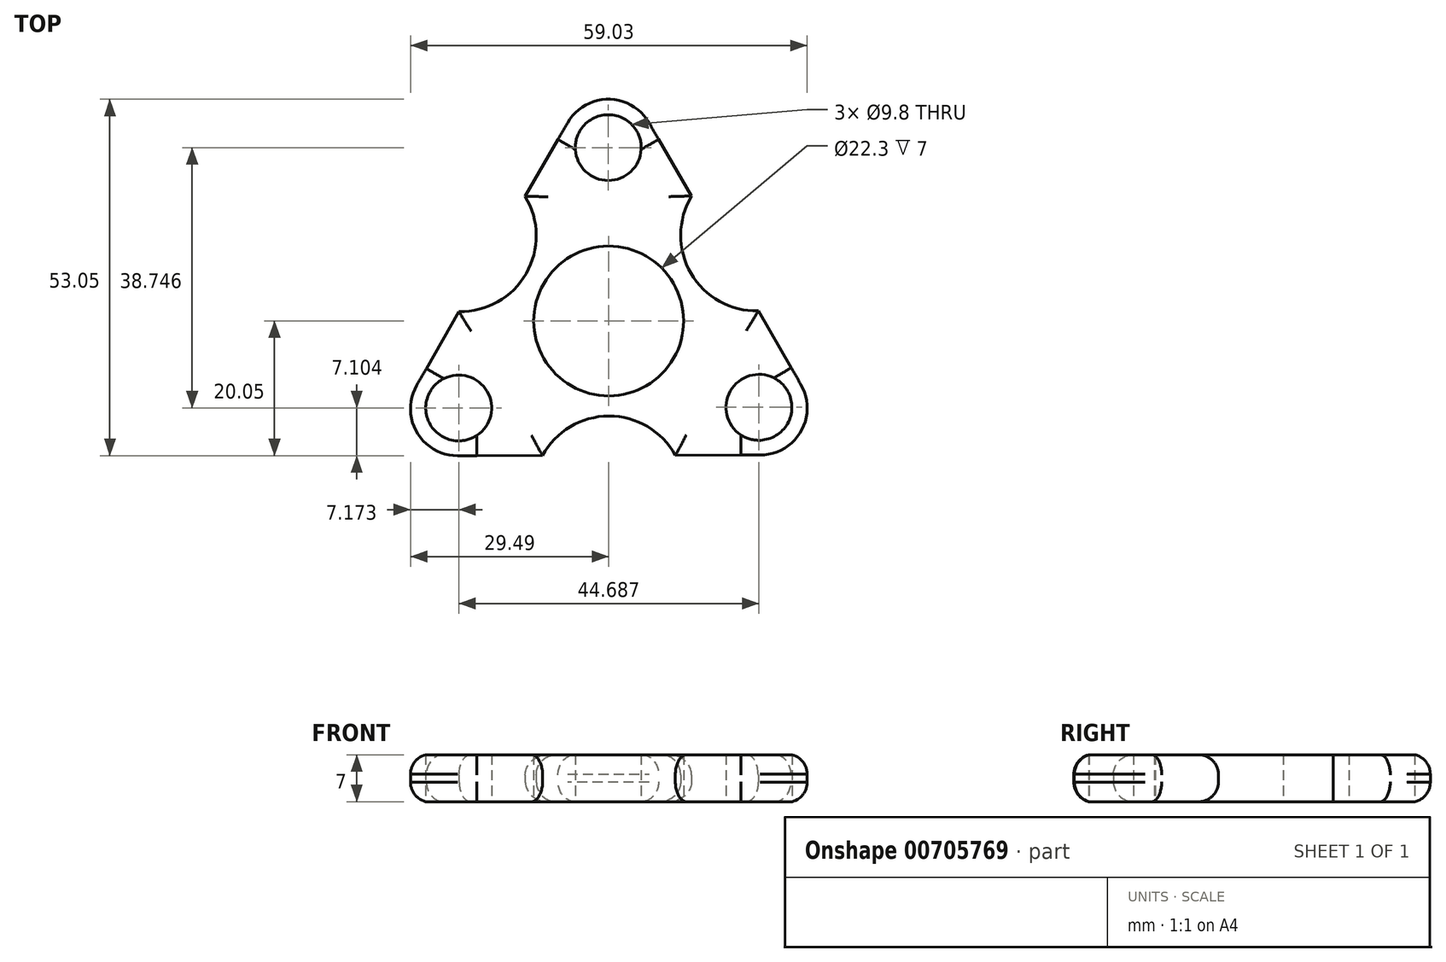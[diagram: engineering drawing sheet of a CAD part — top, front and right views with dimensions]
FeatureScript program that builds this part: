
annotation { "Feature Type Name" : "Feature", "Feature Type Description" : "" }
export const myFeature = defineFeature(function(context is Context, id is Id, definition is map)
    precondition{}
    {
        {
            var Q0;
            Q0=qCreatedBy(makeId("Top.planeOp"),FACE);
            var sketch = newSketch(context, id + "F0", { "sketchPlane" : qUnion([Q0])});
            skCircle(sketch, "E0.cCircle", {"center": v(0, 0) * mm, "radius": 20 * mm, "construction": true});
            skLineSegment(sketch, "E0.0", {"start": v(6, 29.51) * mm, "end": v(28.6, -9.44) * mm});
            skLineSegment(sketch, "E0.1", {"start": v(22.56, -19.95) * mm, "end": v(-22.48, -20.05) * mm});
            skLineSegment(sketch, "E0.2", {"start": v(-28.56, -9.56) * mm, "end": v(-6.12, 29.49) * mm});
            skPoint(sketch, "E0.0.midPoint", {"position": v(17.3, 10.04) * mm});
            skCircle(sketch, "E1", {"center": v(22.37, -12.85) * mm, "radius": 7.1 * mm});
            skCircle(sketch, "E2", {"center": v(22.37, -12.85) * mm, "radius": 4.9 * mm});
            skCircle(sketch, "E3", {"center": v(0, 0) * mm, "radius": 11.15 * mm});
            skArc(sketch, "E4", {"start": v(12.34, 18.58) * mm, "mid": v(12.24, 7.1) * mm, "end": v(22.26, 1.5) * mm});
            skArc(sketch, "E5.1.0", {"start": v(-22.26, 1.4) * mm, "mid": v(-12.27, 7.05) * mm, "end": v(-12.42, 18.53) * mm});
            skPoint(sketch, "E5.1.1", {"position": v(-17.34, 9.96) * mm});
            skCircle(sketch, "E5.1.2", {"center": v(-0.05, 25.8) * mm, "radius": 4.9 * mm});
            skCircle(sketch, "E5.1.3", {"center": v(-0.05, 25.8) * mm, "radius": 7.1 * mm});
            skArc(sketch, "E5.2.0", {"start": v(9.92, -19.98) * mm, "mid": v(0.03, -14.15) * mm, "end": v(-9.83, -20.02) * mm});
            skPoint(sketch, "E5.2.1", {"position": v(0.04, -20) * mm});
            skCircle(sketch, "E5.2.2", {"center": v(-22.32, -12.95) * mm, "radius": 4.9 * mm});
            skCircle(sketch, "E5.2.3", {"center": v(-22.32, -12.95) * mm, "radius": 7.1 * mm});
            skPoint(sketch, "E6.visualSharp", {"position": v(-34.6, -20.07) * mm});
            skArc(sketch, "E6.filletArc", {"start": v(-28.56, -9.56) * mm, "mid": v(-28.54, -16.56) * mm, "end": v(-22.48, -20.05) * mm});
            skPoint(sketch, "E7.visualSharp", {"position": v(-0.08, 40) * mm});
            skArc(sketch, "E7.filletArc", {"start": v(6, 29.51) * mm, "mid": v(-0.07, 33) * mm, "end": v(-6.12, 29.49) * mm});
            skPoint(sketch, "E8.visualSharp", {"position": v(34.68, -19.93) * mm});
            skArc(sketch, "E8.filletArc", {"start": v(22.56, -19.95) * mm, "mid": v(28.61, -16.44) * mm, "end": v(28.6, -9.44) * mm});
            skSolve(sketch);
        }
        {
            var Q0;
            Q0=makeQuery(id+"F0.imprint","IMPRINT",FACE,{"disambiguationData":[TD([[makeQuery(id+"F0.imprint","IMPRINT",EDGE,{"derivedFrom":sQuery(id+"F0.wireOp",EDGE,"E2")}),-1.0]])]});
            var Q1;
            Q1=makeQuery(id+"F0.imprint","IMPRINT",FACE,{"disambiguationData":[TD([[makeQuery(id+"F0.imprint","IMPRINT",EDGE,{"derivedFrom":sQuery(id+"F0.wireOp",EDGE,"E5.1.2")}),-1.0]])]});
            var Q2;
            Q2=makeQuery(id+"F0.imprint","IMPRINT",FACE,{"disambiguationData":[TD([[makeQuery(id+"F0.imprint","IMPRINT",EDGE,{"derivedFrom":sQuery(id+"F0.wireOp",EDGE,"E5.2.2")}),-1.0]])]});
            var Q3;
            {var subQ0=sQuery(id+"F0.wireOp",EDGE,"E8.filletArc");Q3=makeQuery(id+"F0.imprint","IMPRINT",FACE,{"disambiguationData":[TD([[makeQuery(id+"F0.imprint","IMPRINT",EDGE,{"derivedFrom":subQ0}),1.0]])]});}
            var Q4;
            {var subQ0=sQuery(id+"F0.wireOp",EDGE,"E6.filletArc");Q4=makeQuery(id+"F0.imprint","IMPRINT",FACE,{"disambiguationData":[TD([[makeQuery(id+"F0.imprint","IMPRINT",EDGE,{"derivedFrom":subQ0}),1.0]])]});}
            var Q5;
            {var subQ0=sQuery(id+"F0.wireOp",EDGE,"E7.filletArc");Q5=makeQuery(id+"F0.imprint","IMPRINT",FACE,{"disambiguationData":[TD([[makeQuery(id+"F0.imprint","IMPRINT",EDGE,{"derivedFrom":subQ0}),1.0]])]});}
            var Q6;
            Q6=makeQuery(id+"F0.imprint","IMPRINT",FACE,{"disambiguationData":[TD([[makeQuery(id+"F0.imprint","IMPRINT",EDGE,{"derivedFrom":sQuery(id+"F0.wireOp",EDGE,"E3")}),-1.0]])]});
            extrude(context, id + "F1", {"entities" : qUnion([Q0, Q1, Q2, Q3, Q4, Q5, Q6]), "depth" : 7 * mm, "offsetDistance" : 25 * mm});
        }
        {
            var Q0;
            Q0=makeQuery(id+"F1.opExtrude","CAP_EDGE",EDGE,{"disambiguationData":[OSD([sQuery(id+"F0.wireOp",EDGE,"E5.2.0")])],"isStart":false});
            var Q1;
            {var subQ0=sQuery(id+"F0.wireOp",EDGE,"E0.1");Q1=makeQuery(id+"F1.opExtrude","CAP_EDGE",EDGE,{"disambiguationData":[OSD([subQ0]),TDD([makeQuery(id+"F0.imprint","IMPRINT",EDGE,{"disambiguationData":[TD([[makeQuery(id+"F0.imprint","INTERSECT",VERTEX,{"disambiguationData":[OD(1.0)],"derivedFrom":[subQ0,sQuery(id+"F0.wireOp",EDGE,"E5.2.0")]}),-1.0]])],"derivedFrom":subQ0}),makeQuery(id+"F0.imprint","IMPRINT",EDGE,{"disambiguationData":[TD([[makeQuery(id+"F0.imprint","INTERSECT",VERTEX,{"derivedFrom":[subQ0,sQuery(id+"F0.wireOp",EDGE,"E6.filletArc")]}),1.0]])],"derivedFrom":subQ0})])],"isStart":false});}
            var Q2;
            Q2=makeQuery(id+"F1.opExtrude","CAP_EDGE",EDGE,{"disambiguationData":[OSD([sQuery(id+"F0.wireOp",EDGE,"E5.1.0")])],"isStart":false});
            var Q3;
            {var subQ0=sQuery(id+"F0.wireOp",EDGE,"E0.2");Q3=makeQuery(id+"F1.opExtrude","CAP_EDGE",EDGE,{"disambiguationData":[OSD([subQ0]),TDD([makeQuery(id+"F0.imprint","IMPRINT",EDGE,{"disambiguationData":[TD([[makeQuery(id+"F0.imprint","INTERSECT",VERTEX,{"disambiguationData":[OD(1.0)],"derivedFrom":[subQ0,sQuery(id+"F0.wireOp",EDGE,"E5.1.0")]}),-1.0]])],"derivedFrom":subQ0}),makeQuery(id+"F0.imprint","IMPRINT",EDGE,{"disambiguationData":[TD([[makeQuery(id+"F0.imprint","INTERSECT",VERTEX,{"derivedFrom":[subQ0,sQuery(id+"F0.wireOp",EDGE,"E7.filletArc")]}),1.0]])],"derivedFrom":subQ0})])],"isStart":false});}
            var Q4;
            {var subQ0=sQuery(id+"F0.wireOp",EDGE,"E0.0");Q4=makeQuery(id+"F1.opExtrude","CAP_EDGE",EDGE,{"disambiguationData":[OSD([subQ0]),TDD([makeQuery(id+"F0.imprint","IMPRINT",EDGE,{"disambiguationData":[TD([[makeQuery(id+"F0.imprint","INTERSECT",VERTEX,{"disambiguationData":[OD(1.0)],"derivedFrom":[subQ0,sQuery(id+"F0.wireOp",EDGE,"E4")]}),-1.0]])],"derivedFrom":subQ0}),makeQuery(id+"F0.imprint","IMPRINT",EDGE,{"disambiguationData":[TD([[makeQuery(id+"F0.imprint","INTERSECT",VERTEX,{"derivedFrom":[subQ0,sQuery(id+"F0.wireOp",EDGE,"E8.filletArc")]}),1.0]])],"derivedFrom":subQ0})])],"isStart":false});}
            var Q5;
            Q5=makeQuery(id+"F1.opExtrude","CAP_EDGE",EDGE,{"disambiguationData":[OSD([sQuery(id+"F0.wireOp",EDGE,"E4")])],"isStart":false});
            var Q6;
            {var subQ0=sQuery(id+"F0.wireOp",EDGE,"E0.1");Q6=makeQuery(id+"F1.opExtrude","CAP_EDGE",EDGE,{"disambiguationData":[OSD([subQ0]),TDD([makeQuery(id+"F0.imprint","IMPRINT",EDGE,{"disambiguationData":[TD([[makeQuery(id+"F0.imprint","INTERSECT",VERTEX,{"derivedFrom":[subQ0,sQuery(id+"F0.wireOp",EDGE,"E8.filletArc")]}),-1.0]])],"derivedFrom":subQ0}),makeQuery(id+"F0.imprint","IMPRINT",EDGE,{"disambiguationData":[TD([[makeQuery(id+"F0.imprint","INTERSECT",VERTEX,{"disambiguationData":[OD(0.0)],"derivedFrom":[subQ0,sQuery(id+"F0.wireOp",EDGE,"E5.2.0")]}),1.0]])],"derivedFrom":subQ0})])],"isStart":true});}
            var Q7;
            {var subQ0=sQuery(id+"F0.wireOp",EDGE,"E0.0");Q7=makeQuery(id+"F1.opExtrude","CAP_EDGE",EDGE,{"disambiguationData":[OSD([subQ0]),TDD([makeQuery(id+"F0.imprint","IMPRINT",EDGE,{"disambiguationData":[TD([[makeQuery(id+"F0.imprint","INTERSECT",VERTEX,{"derivedFrom":[subQ0,sQuery(id+"F0.wireOp",EDGE,"E7.filletArc")]}),-1.0]])],"derivedFrom":subQ0}),makeQuery(id+"F0.imprint","IMPRINT",EDGE,{"disambiguationData":[TD([[makeQuery(id+"F0.imprint","INTERSECT",VERTEX,{"disambiguationData":[OD(0.0)],"derivedFrom":[subQ0,sQuery(id+"F0.wireOp",EDGE,"E4")]}),1.0]])],"derivedFrom":subQ0})])],"isStart":true});}
            var Q8;
            Q8=makeQuery(id+"F1.opExtrude","CAP_EDGE",EDGE,{"disambiguationData":[OSD([sQuery(id+"F0.wireOp",EDGE,"E5.1.0")])],"isStart":true});
            var Q9;
            {var subQ0=sQuery(id+"F0.wireOp",EDGE,"E0.2");Q9=makeQuery(id+"F1.opExtrude","CAP_EDGE",EDGE,{"disambiguationData":[OSD([subQ0]),TDD([makeQuery(id+"F0.imprint","IMPRINT",EDGE,{"disambiguationData":[TD([[makeQuery(id+"F0.imprint","INTERSECT",VERTEX,{"derivedFrom":[subQ0,sQuery(id+"F0.wireOp",EDGE,"E6.filletArc")]}),-1.0]])],"derivedFrom":subQ0}),makeQuery(id+"F0.imprint","IMPRINT",EDGE,{"disambiguationData":[TD([[makeQuery(id+"F0.imprint","INTERSECT",VERTEX,{"disambiguationData":[OD(0.0)],"derivedFrom":[subQ0,sQuery(id+"F0.wireOp",EDGE,"E5.1.0")]}),1.0]])],"derivedFrom":subQ0})])],"isStart":true});}
            var Q10;
            Q10=makeQuery(id+"F1.opExtrude","CAP_EDGE",EDGE,{"disambiguationData":[OSD([sQuery(id+"F0.wireOp",EDGE,"E6.filletArc")])],"isStart":true});
            var Q11;
            Q11=makeQuery(id+"F1.opExtrude","CAP_EDGE",EDGE,{"disambiguationData":[OSD([sQuery(id+"F0.wireOp",EDGE,"E5.2.0")])],"isStart":true});
            var Q12;
            Q12=makeQuery(id+"F1.opExtrude","CAP_EDGE",EDGE,{"disambiguationData":[OSD([sQuery(id+"F0.wireOp",EDGE,"E4")])],"isStart":true});
            fillet(context, id + "F2", {"entities" : qUnion([Q0, Q1, Q2, Q3, Q4, Q5, Q6, Q7, Q8, Q9, Q10, Q11, Q12]), "radius" : 3 * mm, "tangentPropagation" : true, "allowEdgeOverflow" : false});
        }
    });
